# Revit family: BLS-4A
name_source: partatom
category: Lighting Fixtures
units: mm (PartAtom-declared; Revit-internal decimal feet)

## family parameters
Cut with Voids When Loaded = No
Host = Face
Light Source = Yes
Maintain Annotation Orientation = No
Part Type = Normal
Room Calculation Point = No
Round Connector Dimension = Use Diameter
Shared = No

## types (1)
- BLS-4A
    Color Filter = 16777215
    Default Elevation = 4 '
    Description = solution that integrates the solar panel, battery and LED module 
into a single low-profile fixture. BLS-8A utilitizes battery 
technology that will not drain below 10% capacity to 
ensure reliable re-charge for maximum performance.
    Dimming Lamp Color Temperature Shift = <None>
    Emit from Line Length = 2 '
    Keynote = LUCE SOLARE
    Lamp = LED
    Manufacturer = BEGHELLI
    Model = BLS-4A
    POLE HEIGHT = 7 '
    POLE MATERIAL = BRACKET
    Photometric Web File = BLS-4A-5700°K.ies
    Tilt Angle = 30.00°
    Type Image = BLS-4A IMAGE.png
    Wattage Comments = 22.6W

## geometry (parser evidence)
native form markers: Sweep x15
no freeform markers — native parametric forms only
